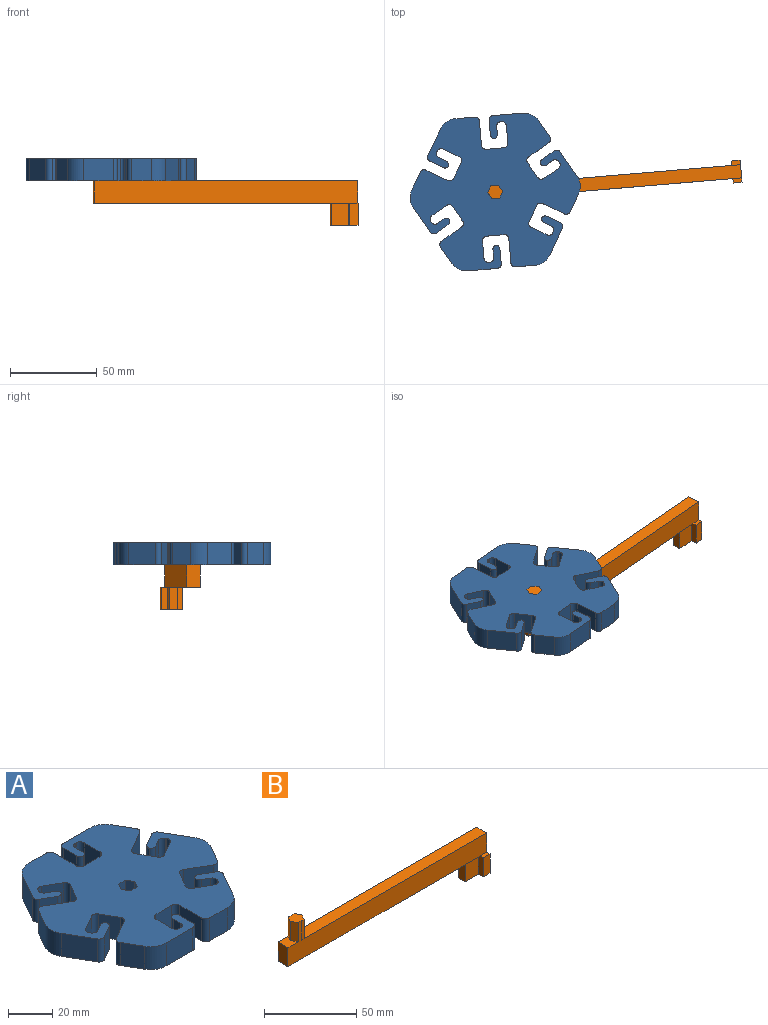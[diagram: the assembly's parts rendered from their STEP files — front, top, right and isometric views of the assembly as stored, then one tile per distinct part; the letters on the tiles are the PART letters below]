
ASSEMBLY  parts=2 mates=1
PART A: 110 faces, bbox 98.5x88x12.7 mm
  f0: plane 98.46x87.99mm, normal (0,0,1), area 5335.3mm2, adj f2,f3,f4,f5,f6,f7,f8,f9
  f1: plane 98.46x87.99mm, normal (0,0,-1), area 5335.3mm2, adj f2,f3,f4,f5,f6,f7,f8,f9
  f2: plane 12.7x11.41mm, normal (0,1,0), area 144.9mm2, adj f0,f1,f50,f103
  f3: plane 14.72x12.7mm, normal (-0.87,0.5,0), area 215.8mm2, adj f0,f1,f50,f56
  f4: plane 12.7x7.26mm, normal (-0.5,-0.87,0), area 106.5mm2, adj f0,f1,f56,f58
  f5: plane 12.7x3.96mm, normal (0.5,0.87,0), area 58.1mm2, adj f0,f1,f57,f59
  f6: plane 12.7x0.44mm, normal (0.87,-0.5,0), area 6.5mm2, adj f0,f1,f59,f60
  f7: plane 12.7x8.8mm, normal (-0.5,-0.87,0), area 129mm2, adj f0,f1,f60,f61
  f8: plane 12.7x8.8mm, normal (-0.87,0.5,0), area 129mm2, adj f0,f1,f61,f62
  f9: plane 12.7x12.1mm, normal (0.5,0.87,0), area 177.4mm2, adj f0,f1,f62,f63
  f10: plane 12.7x9.88mm, normal (-0.87,0.5,0), area 144.9mm2, adj f0,f1,f51,f63
  f11: plane 14.72x12.7mm, normal (-0.87,-0.5,0), area 215.8mm2, adj f0,f1,f51,f64
  f12: plane 12.7x7.26mm, normal (0.5,-0.87,0), area 106.5mm2, adj f0,f1,f64,f66
  f13: plane 12.7x3.96mm, normal (-0.5,0.87,0), area 58.1mm2, adj f0,f1,f65,f67
  f14: plane 12.7x0.44mm, normal (0.87,0.5,0), area 6.5mm2, adj f0,f1,f67,f68
  f15: plane 12.7x8.8mm, normal (0.5,-0.87,0), area 129mm2, adj f0,f1,f68,f69
  f16: plane 12.7x8.8mm, normal (-0.87,-0.5,0), area 129mm2, adj f0,f1,f69,f70
  f17: plane 12.7x12.1mm, normal (-0.5,0.87,0), area 177.4mm2, adj f0,f1,f70,f71
  f18: plane 12.7x9.88mm, normal (-0.87,-0.5,0), area 144.9mm2, adj f0,f1,f52,f71
  f19: plane 16.99x12.7mm, normal (0,-1,0), area 215.8mm2, adj f0,f1,f52,f72
  f20: plane 12.7x8.38mm, normal (1,0,0), area 106.5mm2, adj f0,f1,f72,f74
  f21: plane 12.7x4.57mm, normal (-1,0,0), area 58.1mm2, adj f0,f1,f73,f75
  f22: plane 12.7x0.51mm, normal (0,1,0), area 6.5mm2, adj f0,f1,f75,f76
  f23: plane 12.7x10.16mm, normal (1,0,0), area 129mm2, adj f0,f1,f76,f77
  f24: plane 12.7x10.16mm, normal (0,-1,0), area 129mm2, adj f0,f1,f77,f78
  f25: plane 13.97x12.7mm, normal (-1,0,0), area 177.4mm2, adj f0,f1,f78,f79
  f26: plane 12.7x11.41mm, normal (0,-1,0), area 144.9mm2, adj f0,f1,f53,f79
  f27: plane 14.72x12.7mm, normal (0.87,-0.5,0), area 215.8mm2, adj f0,f1,f53,f80
  f28: plane 12.7x7.26mm, normal (0.5,0.87,0), area 106.5mm2, adj f0,f1,f80,f82
  f29: plane 12.7x3.96mm, normal (-0.5,-0.87,0), area 58.1mm2, adj f0,f1,f81,f83
  f30: plane 12.7x0.44mm, normal (-0.87,0.5,0), area 6.5mm2, adj f0,f1,f83,f84
  f31: plane 12.7x8.8mm, normal (0.5,0.87,0), area 129mm2, adj f0,f1,f84,f85
  f32: plane 12.7x8.8mm, normal (0.87,-0.5,0), area 129mm2, adj f0,f1,f85,f86
  f33: plane 12.7x12.1mm, normal (-0.5,-0.87,0), area 177.4mm2, adj f0,f1,f86,f87
  f34: plane 12.7x9.88mm, normal (0.87,-0.5,0), area 144.9mm2, adj f0,f1,f54,f87
  f35: plane 14.72x12.7mm, normal (0.87,0.5,0), area 215.8mm2, adj f0,f1,f54,f88
  f36: plane 12.7x7.26mm, normal (-0.5,0.87,0), area 106.5mm2, adj f0,f1,f88,f90
  f37: plane 12.7x3.96mm, normal (0.5,-0.87,0), area 58.1mm2, adj f0,f1,f89,f91
  f38: plane 12.7x0.44mm, normal (-0.87,-0.5,0), area 6.5mm2, adj f0,f1,f91,f92
  f39: plane 12.7x8.8mm, normal (-0.5,0.87,0), area 129mm2, adj f0,f1,f92,f93
  f40: plane 12.7x8.8mm, normal (0.87,0.5,0), area 129mm2, adj f0,f1,f93,f94
  f41: plane 12.7x12.1mm, normal (0.5,-0.87,0), area 177.4mm2, adj f0,f1,f94,f95
  f42: plane 12.7x9.88mm, normal (0.87,0.5,0), area 144.9mm2, adj f0,f1,f55,f95
  f43: plane 16.99x12.7mm, normal (0,1,0), area 215.8mm2, adj f0,f1,f55,f96
  f44: plane 12.7x8.38mm, normal (-1,0,0), area 106.5mm2, adj f0,f1,f96,f98
  f45: plane 12.7x4.57mm, normal (1,0,0), area 58.1mm2, adj f0,f1,f97,f99
  f46: plane 12.7x0.51mm, normal (0,-1,0), area 6.5mm2, adj f0,f1,f99,f100
  f47: plane 12.7x10.16mm, normal (-1,0,0), area 129mm2, adj f0,f1,f100,f101
  f48: plane 12.7x10.16mm, normal (0,1,0), area 129mm2, adj f0,f1,f101,f102
  f49: plane 13.97x12.7mm, normal (1,0,0), area 177.4mm2, adj f0,f1,f102,f103
  f50: cylinder r=10.16mm len=12.7mm, axis (0,0,-1), area 135.1mm2, adj f0,f1,f2,f3
  f51: cylinder r=10.16mm len=12.7mm, axis (0,0,-1), area 135.1mm2, adj f0,f1,f10,f11
  f52: cylinder r=10.16mm len=12.7mm, axis (0,0,-1), area 135.1mm2, adj f0,f1,f18,f19
  f53: cylinder r=10.16mm len=12.7mm, axis (0,0,-1), area 135.1mm2, adj f0,f1,f26,f27
  f54: cylinder r=10.16mm len=12.7mm, axis (0,0,-1), area 135.1mm2, adj f0,f1,f34,f35
  f55: cylinder r=10.16mm len=12.7mm, axis (0,0,-1), area 135.1mm2, adj f0,f1,f42,f43
  f56: cylinder r=2.54mm len=12.7mm, axis (0,0,-1), area 50.7mm2, adj f0,f1,f3,f4
  f57: cylinder r=2.54mm len=12.7mm, axis (0,0,-1), area 44.2mm2, adj f0,f1,f5,f58
  f58: cylinder r=2.54mm len=12.7mm, axis (0,0,-1), area 44.2mm2, adj f0,f1,f4,f57
  f59: cylinder r=2.54mm len=12.7mm, axis (0,0,1), area 50.7mm2, adj f0,f1,f5,f6
  f60: cylinder r=2.54mm len=12.7mm, axis (0,0,1), area 50.7mm2, adj f0,f1,f6,f7
  f61: cylinder r=2.54mm len=12.7mm, axis (0,0,1), area 50.7mm2, adj f0,f1,f7,f8
  f62: cylinder r=2.54mm len=12.7mm, axis (0,0,1), area 50.7mm2, adj f0,f1,f8,f9
  f63: cylinder r=2.54mm len=12.7mm, axis (0,0,-1), area 50.7mm2, adj f0,f1,f9,f10
  f64: cylinder r=2.54mm len=12.7mm, axis (0,0,-1), area 50.7mm2, adj f0,f1,f11,f12
  f65: cylinder r=2.54mm len=12.7mm, axis (0,0,-1), area 44.2mm2, adj f0,f1,f13,f66
  f66: cylinder r=2.54mm len=12.7mm, axis (0,0,-1), area 44.2mm2, adj f0,f1,f12,f65
  f67: cylinder r=2.54mm len=12.7mm, axis (0,0,1), area 50.7mm2, adj f0,f1,f13,f14
  f68: cylinder r=2.54mm len=12.7mm, axis (0,0,1), area 50.7mm2, adj f0,f1,f14,f15
  f69: cylinder r=2.54mm len=12.7mm, axis (0,0,1), area 50.7mm2, adj f0,f1,f15,f16
  f70: cylinder r=2.54mm len=12.7mm, axis (0,0,1), area 50.7mm2, adj f0,f1,f16,f17
  f71: cylinder r=2.54mm len=12.7mm, axis (0,0,-1), area 50.7mm2, adj f0,f1,f17,f18
  f72: cylinder r=2.54mm len=12.7mm, axis (0,0,-1), area 50.7mm2, adj f0,f1,f19,f20
  f73: cylinder r=2.54mm len=12.7mm, axis (0,0,-1), area 44.2mm2, adj f0,f1,f21,f74
  f74: cylinder r=2.54mm len=12.7mm, axis (0,0,-1), area 44.2mm2, adj f0,f1,f20,f73
  f75: cylinder r=2.54mm len=12.7mm, axis (0,0,1), area 50.7mm2, adj f0,f1,f21,f22
  f76: cylinder r=2.54mm len=12.7mm, axis (0,0,1), area 50.7mm2, adj f0,f1,f22,f23
  f77: cylinder r=2.54mm len=12.7mm, axis (0,0,1), area 50.7mm2, adj f0,f1,f23,f24
  f78: cylinder r=2.54mm len=12.7mm, axis (0,0,1), area 50.7mm2, adj f0,f1,f24,f25
  f79: cylinder r=2.54mm len=12.7mm, axis (0,0,-1), area 50.7mm2, adj f0,f1,f25,f26
  f80: cylinder r=2.54mm len=12.7mm, axis (0,0,-1), area 50.7mm2, adj f0,f1,f27,f28
  f81: cylinder r=2.54mm len=12.7mm, axis (0,0,-1), area 44.2mm2, adj f0,f1,f29,f82
  f82: cylinder r=2.54mm len=12.7mm, axis (0,0,-1), area 44.2mm2, adj f0,f1,f28,f81
  f83: cylinder r=2.54mm len=12.7mm, axis (0,0,1), area 50.7mm2, adj f0,f1,f29,f30
  f84: cylinder r=2.54mm len=12.7mm, axis (0,0,1), area 50.7mm2, adj f0,f1,f30,f31
  f85: cylinder r=2.54mm len=12.7mm, axis (0,0,1), area 50.7mm2, adj f0,f1,f31,f32
  f86: cylinder r=2.54mm len=12.7mm, axis (0,0,1), area 50.7mm2, adj f0,f1,f32,f33
  f87: cylinder r=2.54mm len=12.7mm, axis (0,0,-1), area 50.7mm2, adj f0,f1,f33,f34
  f88: cylinder r=2.54mm len=12.7mm, axis (0,0,-1), area 50.7mm2, adj f0,f1,f35,f36
  f89: cylinder r=2.54mm len=12.7mm, axis (0,0,-1), area 44.2mm2, adj f0,f1,f37,f90
  f90: cylinder r=2.54mm len=12.7mm, axis (0,0,-1), area 44.2mm2, adj f0,f1,f36,f89
  f91: cylinder r=2.54mm len=12.7mm, axis (0,0,1), area 50.7mm2, adj f0,f1,f37,f38
  f92: cylinder r=2.54mm len=12.7mm, axis (0,0,1), area 50.7mm2, adj f0,f1,f38,f39
  f93: cylinder r=2.54mm len=12.7mm, axis (0,0,1), area 50.7mm2, adj f0,f1,f39,f40
  f94: cylinder r=2.54mm len=12.7mm, axis (0,0,1), area 50.7mm2, adj f0,f1,f40,f41
  f95: cylinder r=2.54mm len=12.7mm, axis (0,0,-1), area 50.7mm2, adj f0,f1,f41,f42
  f96: cylinder r=2.54mm len=12.7mm, axis (0,0,-1), area 50.7mm2, adj f0,f1,f43,f44
  f97: cylinder r=2.54mm len=12.7mm, axis (0,0,-1), area 44.2mm2, adj f0,f1,f45,f98
  f98: cylinder r=2.54mm len=12.7mm, axis (0,0,-1), area 44.2mm2, adj f0,f1,f44,f97
  f99: cylinder r=2.54mm len=12.7mm, axis (0,0,1), area 50.7mm2, adj f0,f1,f45,f46
  f100: cylinder r=2.54mm len=12.7mm, axis (0,0,1), area 50.7mm2, adj f0,f1,f46,f47
  f101: cylinder r=2.54mm len=12.7mm, axis (0,0,1), area 50.7mm2, adj f0,f1,f47,f48
  f102: cylinder r=2.54mm len=12.7mm, axis (0,0,1), area 50.7mm2, adj f0,f1,f48,f49
  f103: cylinder r=2.54mm len=12.7mm, axis (0,0,-1), area 50.7mm2, adj f0,f1,f2,f49
  f104: plane 12.7x3.81mm, normal (-0.87,-0.5,0), area 55.9mm2, adj f0,f1,f105,f109
  f105: plane 12.7x4.4mm, normal (0,-1,0), area 55.9mm2, adj f0,f1,f104,f106
  f106: plane 12.7x3.81mm, normal (0.87,-0.5,0), area 55.9mm2, adj f0,f1,f105,f107
  f107: plane 12.7x3.81mm, normal (0.87,0.5,0), area 55.9mm2, adj f0,f1,f106,f108
  f108: plane 12.7x4.4mm, normal (0,1,0), area 55.9mm2, adj f0,f1,f107,f109
  f109: plane 12.7x3.81mm, normal (-0.87,0.5,0), area 55.9mm2, adj f0,f1,f104,f108
PART B: 24 faces, bbox 152.4x12.7x38.1 mm
  f0: plane 7.93x7.62mm, normal (0,0,1), area 52mm2, adj f3,f4,f6,f21,f22
  f1: plane 140.07x7.62mm, normal (0,0,1), area 1059mm2, adj f4,f5,f6,f18,f19
  f2: plane 147.32x7.62mm, normal (0,0,-1), area 1071mm2, adj f3,f4,f6,f9,f10,f11,f12,f13
  f3: plane 12.7x7.62mm, normal (-1,0,0), area 96.8mm2, adj f0,f2,f4,f6
  f4: plane 152.41x25.41mm, normal (0,-1,0), area 1963.4mm2, adj f0,f1,f2,f3,f5,f7,f17,f22
  f5: plane 25.4x12.7mm, normal (1,0,0), area 258.1mm2, adj f1,f4,f6,f7,f8,f14,f15,f16
  f6: plane 152.41x25.41mm, normal (0,1,0), area 1963.4mm2, adj f0,f1,f2,f3,f5,f16,f19,f20
  f7: plane 5.08x2.54mm, normal (0,0,1), area 12.9mm2, adj f4,f5,f8,f9
  f8: plane 12.7x5.08mm, normal (0,-1,0), area 64.5mm2, adj f5,f7,f9,f15
  f9: plane 12.7x3.81mm, normal (-1,0,0), area 48.4mm2, adj f2,f7,f8,f10,f15
  f10: plane 12.7x10.16mm, normal (0,-1,0), area 129mm2, adj f2,f9,f11,f15
  f11: plane 12.7x5.08mm, normal (-1,0,0), area 64.5mm2, adj f2,f10,f12,f15
  f12: plane 12.7x10.16mm, normal (0,1,0), area 129mm2, adj f2,f11,f13,f15
  f13: plane 12.7x3.81mm, normal (-1,0,0), area 48.4mm2, adj f2,f12,f14,f15,f16
  f14: plane 12.7x5.08mm, normal (0,1,0), area 64.5mm2, adj f5,f13,f15,f16
  f15: plane 15.24x12.7mm, normal (0,0,-1), area 116.1mm2, adj f5,f8,f9,f10,f11,f12,f13,f14
  f16: plane 5.08x2.54mm, normal (0,0,1), area 12.9mm2, adj f5,f6,f13,f14
  f17: plane 12.71x2.21mm, normal (0,-1,0), area 28mm2, adj f4,f18,f23
  f18: plane 12.7x3.82mm, normal (0.87,-0.5,0), area 55.9mm2, adj f1,f17,f19,f23
  f19: plane 12.7x3.8mm, normal (0.87,0.5,0), area 55.8mm2, adj f1,f6,f18,f23
  f20: plane 12.71x2.21mm, normal (0,1,0), area 28mm2, adj f6,f21,f23
  f21: plane 12.7x3.82mm, normal (-0.87,0.5,0), area 55.9mm2, adj f0,f20,f22,f23
  f22: plane 12.7x3.8mm, normal (-0.87,-0.5,0), area 55.8mm2, adj f0,f4,f21,f23
  f23: plane 8.8x7.62mm, normal (0,0,1), area 50.3mm2, adj f4,f6,f17,f18,f19,f20,f21,f22
PLACE A rot(axis=(0,0,1),4.8deg) t=(-152.58,8.88,-1)mm
PLACE B rot(axis=(0,0,1),4.8deg) t=(-145.95,9.43,-1)mm
MATE fastened B.f23 <-> A.f0  axis (0,0,1) through (-148.19,9.25,11.7)mm
